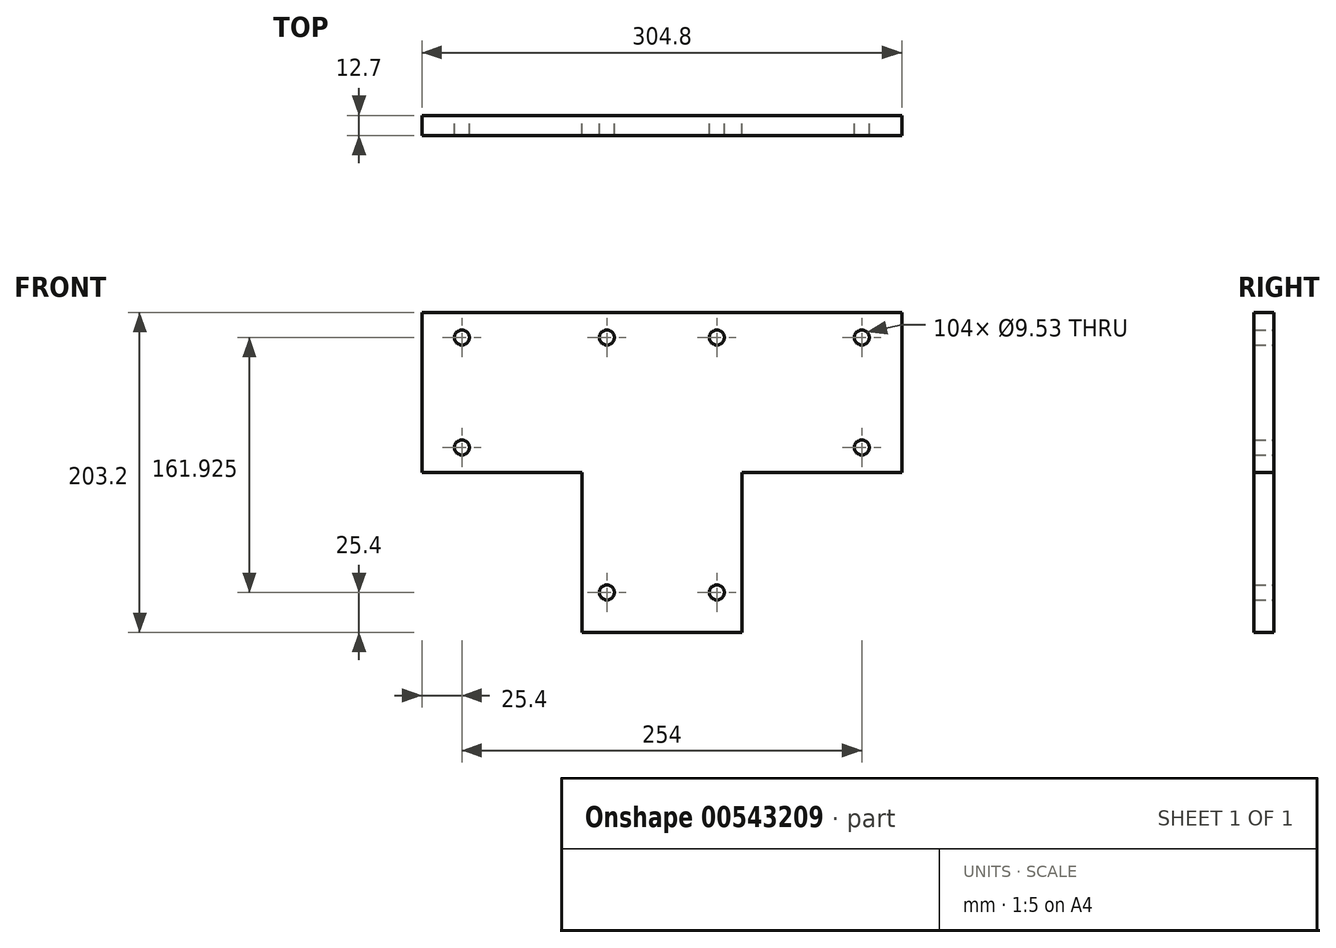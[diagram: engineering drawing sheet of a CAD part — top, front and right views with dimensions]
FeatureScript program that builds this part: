
annotation { "Feature Type Name" : "Feature", "Feature Type Description" : "" }
export const myFeature = defineFeature(function(context is Context, id is Id, definition is map)
    precondition{}
    {
        {
            var Q0;
            Q0=qCreatedBy(makeId("Front.planeOp"),FACE);
            var sketch = newSketch(context, id + "F0", { "sketchPlane" : qUnion([Q0])});
            skLineSegment(sketch, "E0.bottom", {"start": v(50.8, 101.6) * mm, "end": v(-50.8, 101.6) * mm});
            skLineSegment(sketch, "E0.top", {"start": v(50.8, -101.6) * mm, "end": v(-50.8, -101.6) * mm});
            skLineSegment(sketch, "E0.left", {"start": v(50.8, 101.6) * mm, "end": v(50.8, -101.6) * mm});
            skLineSegment(sketch, "E0.right", {"start": v(-50.8, 101.6) * mm, "end": v(-50.8, -101.6) * mm});
            skPoint(sketch, "E0.middle", {"position": v(0, 0) * mm});
            skLineSegment(sketch, "E1.bottom", {"start": v(50.8, 101.6) * mm, "end": v(152.4, 101.6) * mm});
            skLineSegment(sketch, "E1.top", {"start": v(50.8, 0) * mm, "end": v(152.4, 0) * mm});
            skLineSegment(sketch, "E1.left", {"start": v(50.8, 101.6) * mm, "end": v(50.8, 0) * mm});
            skLineSegment(sketch, "E1.right", {"start": v(152.4, 101.6) * mm, "end": v(152.4, 0) * mm});
            skLineSegment(sketch, "E2.MirrorCS", {"start": v(-50.8, 101.6) * mm, "end": v(-152.4, 101.6) * mm});
            skLineSegment(sketch, "E3.MirrorCS", {"start": v(-152.4, 101.6) * mm, "end": v(-152.4, 0) * mm});
            skLineSegment(sketch, "E4.MirrorCS", {"start": v(-50.8, 0) * mm, "end": v(-152.4, 0) * mm});
            skLineSegment(sketch, "E5.MirrorCS", {"start": v(-50.8, 101.6) * mm, "end": v(-50.8, 0) * mm});
            skLineSegment(sketch, "E6", {"start": v(-50.8, 76.2) * mm, "end": v(50.8, 76.2) * mm, "construction": true});
            skLineSegment(sketch, "E7.MirrorCS", {"start": v(-50.8, -76.2) * mm, "end": v(50.8, -76.2) * mm, "construction": true});
            skLineSegment(sketch, "E8", {"start": v(-127, 101.6) * mm, "end": v(-127, 0) * mm, "construction": true});
            skLineSegment(sketch, "E9.MirrorCS", {"start": v(127, 101.6) * mm, "end": v(127, 0) * mm, "construction": true});
            skLineSegment(sketch, "E10", {"start": v(-152.4, 50.8) * mm, "end": v(152.4, 50.8) * mm});
            skLineSegment(sketch, "E11", {"start": v(-152.4, 85.72) * mm, "end": v(152.4, 85.73) * mm, "construction": true});
            skLineSegment(sketch, "E12.MirrorCS", {"start": v(-152.4, 15.88) * mm, "end": v(152.4, 15.87) * mm, "construction": true});
            skCircle(sketch, "E13", {"center": v(-127, 85.72) * mm, "radius": 4.76 * mm});
            skCircle(sketch, "E14", {"center": v(-127, 15.88) * mm, "radius": 4.76 * mm});
            skCircle(sketch, "E15.MirrorC", {"center": v(127, 15.88) * mm, "radius": 4.76 * mm});
            skCircle(sketch, "E16.MirrorC", {"center": v(127, 85.72) * mm, "radius": 4.76 * mm});
            skCircle(sketch, "E17", {"center": v(34.93, -76.2) * mm, "radius": 4.76 * mm});
            skCircle(sketch, "E18.MirrorC", {"center": v(-34.93, -76.2) * mm, "radius": 4.76 * mm});
            skLineSegment(sketch, "E19", {"start": v(34.93, -76.2) * mm, "end": v(34.93, 101.6) * mm, "construction": true});
            skLineSegment(sketch, "E20", {"start": v(-34.93, -76.2) * mm, "end": v(-34.93, 101.6) * mm, "construction": true});
            skCircle(sketch, "E21", {"center": v(-34.93, 85.73) * mm, "radius": 4.76 * mm});
            skCircle(sketch, "E22.MirrorC", {"center": v(34.93, 85.73) * mm, "radius": 4.76 * mm});
            skSolve(sketch);
        }
        {
            var Q0;
            Q0 = qSketchRegion(id + "F0", true);
            extrude(context, id + "F1", {"entities" : qUnion([Q0]), "depth" : 12.7 * mm, "offsetDistance" : 25.4 * mm});
        }
    });
